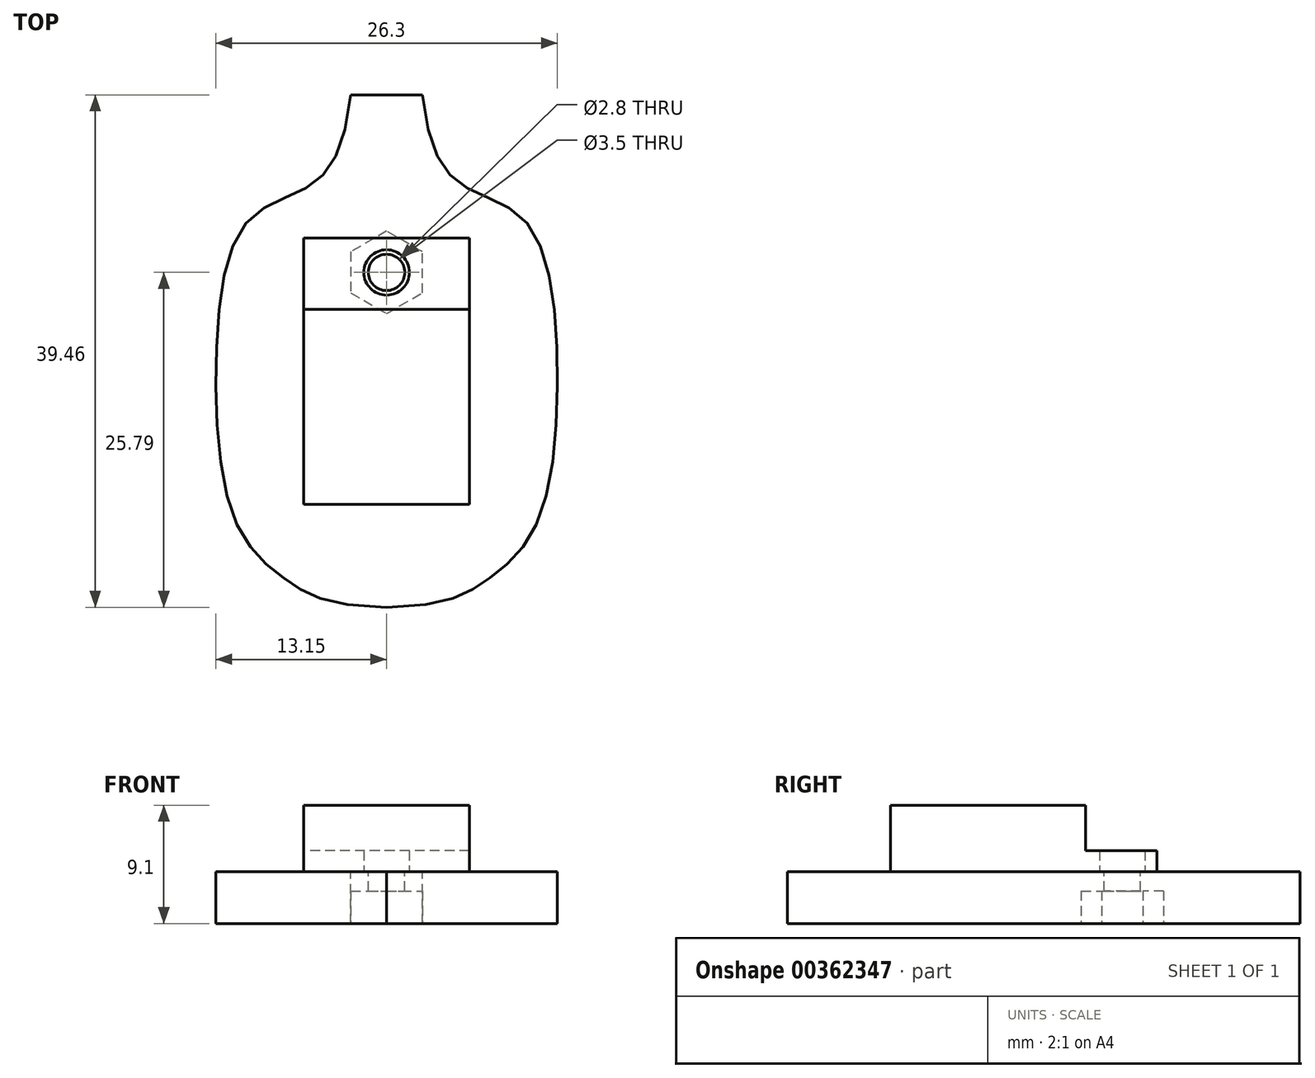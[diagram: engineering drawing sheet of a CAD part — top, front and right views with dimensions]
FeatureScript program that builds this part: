
annotation { "Feature Type Name" : "Feature", "Feature Type Description" : "" }
export const myFeature = defineFeature(function(context is Context, id is Id, definition is map)
    precondition{}
    {
        {
            var Q0;
            Q0=qCreatedBy(makeId("Top.planeOp"),FACE);
            var sketch = newSketch(context, id + "F0", { "sketchPlane" : qUnion([Q0])});
            skLineSegment(sketch, "E0.bottom", {"start": v(6.37, 10.25) * mm, "end": v(-6.38, 10.25) * mm});
            skLineSegment(sketch, "E0.top", {"start": v(6.38, -10.25) * mm, "end": v(-6.37, -10.25) * mm});
            skLineSegment(sketch, "E0.left", {"start": v(6.37, 10.25) * mm, "end": v(6.38, -10.25) * mm});
            skLineSegment(sketch, "E0.right", {"start": v(-6.38, 10.25) * mm, "end": v(-6.37, -10.25) * mm});
            skPoint(sketch, "E0.middle", {"position": v(0, 0) * mm});
            skCircle(sketch, "E1", {"center": v(0, 7.6) * mm, "radius": 1.75 * mm});
            skSolve(sketch);
        }
        {
            var Q0;
            Q0 = qSketchRegion(id + "F0", true);
            extrude(context, id + "F1", {"entities" : qUnion([Q0]), "depth" : 1.6 * mm});
        }
        {
            var Q0;
            Q0=makeQuery(id+"F1.opExtrude","CAP_FACE",FACE,{"disambiguationData":[OSD([sQuery(id+"F0.wireOp",EDGE,"E0.bottom"),sQuery(id+"F0.wireOp",EDGE,"E0.top"),sQuery(id+"F0.wireOp",EDGE,"E0.left"),sQuery(id+"F0.wireOp",EDGE,"E0.right"),sQuery(id+"F0.wireOp",EDGE,"E1")])],"isStart":true});
            var sketch = newSketch(context, id + "F2", { "sketchPlane" : qUnion([Q0])});
            skCircle(sketch, "E2", {"center": v(0, -7.6) * mm, "radius": 1.4 * mm});
            skLineSegment(sketch, "E3", {"start": v(-2.75, -21.27) * mm, "end": v(2.75, -21.27) * mm});
            skFitSpline(sketch, "E4", {"points": [v(2.75, -21.27) * mm, v(5.72, -14.4) * mm, v(10.62, -11.62) * mm, v(13.11, -1.35) * mm, v(11.48, 11.9) * mm, v(7.63, 16.14) * mm, v(0, 18.2) * mm], "startDerivative": vector(7.63, 70.06) * mm, "endDerivative": vector(-82.25, 0.92) * mm});
            skFitSpline(sketch, "E5.MirrorCS", {"points": [v(-2.75, -21.27) * mm, v(-5.72, -14.4) * mm, v(-10.62, -11.62) * mm, v(-13.11, -1.35) * mm, v(-11.48, 11.9) * mm, v(-7.63, 16.14) * mm, v(0, 18.2) * mm], "startDerivative": vector(-7.63, 70.06) * mm, "endDerivative": vector(82.25, 0.92) * mm});
            skLineSegment(sketch, "E6.0", {"start": v(-10.87, 14.75) * mm, "end": v(10.88, 14.75) * mm, "construction": true});
            skLineSegment(sketch, "E6.1", {"start": v(-10.88, -14.75) * mm, "end": v(-10.87, 14.75) * mm, "construction": true});
            skLineSegment(sketch, "E6.2", {"start": v(10.87, -14.75) * mm, "end": v(-10.88, -14.75) * mm, "construction": true});
            skLineSegment(sketch, "E6.3", {"start": v(10.88, 14.75) * mm, "end": v(10.87, -14.75) * mm, "construction": true});
            skSolve(sketch);
        }
        {
            var Q0;
            Q0 = qSketchRegion(id + "F2", true);
            extrude(context, id + "F3", {"entities" : qUnion([Q0]), "depth" : 4 * mm});
        }
        {
            var Q0;
            Q0=makeQuery(id+"F3.opExtrude","CAP_FACE",FACE,{"disambiguationData":[OSD([sQuery(id+"F2.wireOp",EDGE,"68caaebf-f82f-4ba4-966e-2a4588f8268f.0"),sQuery(id+"F2.wireOp",EDGE,"68caaebf-f82f-4ba4-966e-2a4588f8268f.1"),sQuery(id+"F2.wireOp",EDGE,"68caaebf-f82f-4ba4-966e-2a4588f8268f.2"),sQuery(id+"F2.wireOp",EDGE,"68caaebf-f82f-4ba4-966e-2a4588f8268f.3"),sQuery(id+"F2.wireOp",EDGE,"E2")])],"isStart":false});
            var sketch = newSketch(context, id + "F4", { "sketchPlane" : qUnion([Q0])});
            skCircle(sketch, "E7.cCircle", {"center": v(0, -7.6) * mm, "radius": 2.75 * mm, "construction": true});
            skLineSegment(sketch, "E7.0", {"start": v(2.75, -6.01) * mm, "end": v(2.75, -9.19) * mm});
            skLineSegment(sketch, "E7.1", {"start": v(2.75, -9.19) * mm, "end": v(0, -10.78) * mm});
            skLineSegment(sketch, "E7.2", {"start": v(0, -10.78) * mm, "end": v(-2.75, -9.19) * mm});
            skLineSegment(sketch, "E7.3", {"start": v(-2.75, -9.19) * mm, "end": v(-2.75, -6.01) * mm});
            skLineSegment(sketch, "E7.4", {"start": v(-2.75, -6.01) * mm, "end": v(0, -4.42) * mm});
            skLineSegment(sketch, "E7.5", {"start": v(0, -4.42) * mm, "end": v(2.75, -6.01) * mm});
            skPoint(sketch, "E7.0.midPoint", {"position": v(2.75, -7.6) * mm});
            skSolve(sketch);
        }
        {
            var Q0;
            Q0 = qSketchRegion(id + "F4", true);
            extrude(context, id + "F5", {"entities" : qUnion([Q0]), "operationType" : NewBodyOperationType.REMOVE, "oppositeDirection" : true, "depth" : 2.5 * mm});
        }
        {
            var Q0;
            Q0=makeQuery(id+"F1.opExtrude","CAP_FACE",FACE,{"disambiguationData":[OSD([sQuery(id+"F0.wireOp",EDGE,"E0.bottom"),sQuery(id+"F0.wireOp",EDGE,"E0.top"),sQuery(id+"F0.wireOp",EDGE,"E0.left"),sQuery(id+"F0.wireOp",EDGE,"E0.right"),sQuery(id+"F0.wireOp",EDGE,"E1")])],"isStart":false});
            var sketch = newSketch(context, id + "F6", { "sketchPlane" : qUnion([Q0])});
            skLineSegment(sketch, "E8.bottom", {"start": v(6.37, 4.75) * mm, "end": v(-6.38, 4.75) * mm});
            skLineSegment(sketch, "E8.top", {"start": v(6.38, -10.25) * mm, "end": v(-6.37, -10.25) * mm});
            skLineSegment(sketch, "E8.left", {"start": v(6.38, 4.75) * mm, "end": v(6.38, -10.25) * mm});
            skLineSegment(sketch, "E8.right", {"start": v(-6.38, 4.75) * mm, "end": v(-6.38, -10.25) * mm});
            skPoint(sketch, "E8.middle", {"position": v(0, -2.75) * mm});
            skSolve(sketch);
        }
        {
            var Q0;
            Q0 = qSketchRegion(id + "F6", true);
            extrude(context, id + "F7", {"entities" : qUnion([Q0]), "operationType" : NewBodyOperationType.ADD, "depth" : 3.5 * mm});
        }
    });
